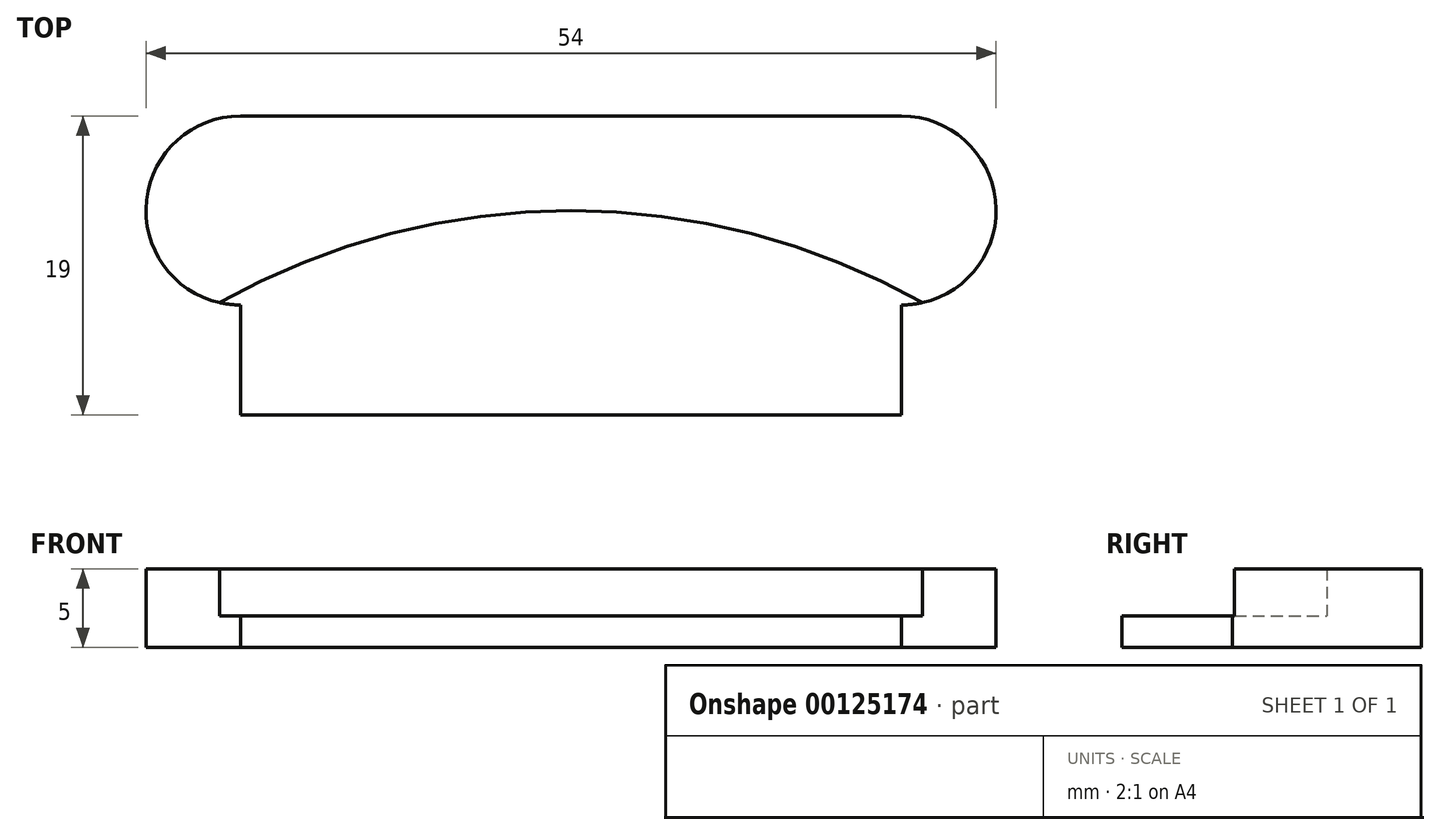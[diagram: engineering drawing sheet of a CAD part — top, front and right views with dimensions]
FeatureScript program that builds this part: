
annotation { "Feature Type Name" : "Feature", "Feature Type Description" : "" }
export const myFeature = defineFeature(function(context is Context, id is Id, definition is map)
    precondition{}
    {
        {
            var Q0;
            Q0=qCreatedBy(makeId("Top.planeOp"),FACE);
            var sketch = newSketch(context, id + "F0", { "sketchPlane" : qUnion([Q0])});
            skArc(sketch, "E0", {"start": v(22.32, 39.65) * mm, "mid": v(0, 45.5) * mm, "end": v(-22.32, 39.65) * mm});
            skLineSegment(sketch, "E1.bottom", {"start": v(21, 51.5) * mm, "end": v(-21, 51.5) * mm});
            skPoint(sketch, "E1.middle", {"position": v(0, 45.5) * mm});
            skArc(sketch, "E2", {"start": v(21, 39.5) * mm, "mid": v(27, 45.5) * mm, "end": v(21, 51.5) * mm});
            skArc(sketch, "E3", {"start": v(-21, 51.5) * mm, "mid": v(-27, 45.5) * mm, "end": v(-21, 39.5) * mm});
            skLineSegment(sketch, "E4", {"start": v(-21, 39.5) * mm, "end": v(-21, 32.5) * mm});
            skLineSegment(sketch, "E5", {"start": v(-21, 32.5) * mm, "end": v(21, 32.5) * mm});
            skLineSegment(sketch, "E6", {"start": v(21, 32.5) * mm, "end": v(21, 39.5) * mm});
            skSolve(sketch);
        }
        {
            var Q0;
            {var subQ0=sQuery(id+"F0.wireOp",EDGE,"E0");Q0=makeQuery(id+"F0.imprint","IMPRINT",FACE,{"disambiguationData":[TD([[makeQuery(id+"F0.imprint","IMPRINT",EDGE,{"derivedFrom":subQ0}),-1.0]])]});}
            extrude(context, id + "F1", {"entities" : qUnion([Q0]), "depth" : 5 * mm});
        }
        {
            var Q0;
            {var subQ2=sQuery(id+"F0.wireOp",EDGE,"E0");Q0=makeQuery(id+"F0.imprint","IMPRINT",FACE,{"disambiguationData":[TD([[makeQuery(id+"F0.imprint","IMPRINT",EDGE,{"derivedFrom":subQ2}),1.0]])]});}
            extrude(context, id + "F2", {"entities" : qUnion([Q0]), "operationType" : NewBodyOperationType.ADD, "depth" : 2 * mm});
        }
    });
